# Revit family: Two Handle Lavatory Faucet_TOTO_TLG03201
name_source: partatom
category: 衛生器具
revit_build: Autodesk Revit 2018 (Build: 20181011_1500(x64)
units: mm (PartAtom-declared; Revit-internal decimal feet)

## family parameters
OmniClass タイトル = Sanitary, Laundry, and Cleaning Equipment
OmniClass 番号 = 23.45.00.00
パーツ タイプ = 標準
ロード時にボイドで切り取り = いいえ
丸型コネクタ寸法 = 直径を使用
作業面ベース = いいえ
共有 = いいえ
常に垂直 = はい
部屋計算ポイント = いいえ

## types (1)
- Two Handle Lavatory Faucet_TOTO_TLG03201
    Finish = faucet_material
    Height = 121.7
    Length = 179.4
    TOTO AsiaOceania = TLG03201B
    TOTO AsiaOceania URL = http://asia.toto.com
    TOTO China = TLG03201B
    TOTO China URL = http://www.toto.com.cn
    TOTO HongKong = TLG03201B
    TOTO HongKong URL = http://hk.toto.com
    TOTO India = TLG03201B
    TOTO India URL = https://in.toto.com
    TOTO Korea = TLG03201K
    TOTO Korea URL = https://kr.toto.com
    TOTO Taiwan = TLG03201B
    TOTO Taiwan URL = https://www.twtoto.com.tw
    TOTO Thailand = TLG03201T
    TOTO Thailand URL = https://th.toto.com
    TOTO USA = TLG03201U
    TOTO USA URL = https://www.totousa.com
    TOTO Vietnam = TLG03201B
    TOTO Vietnam URL = https://vn.toto.com
    Width = 341.1
    モデル = TLG03201
    製造元 = TOTO Ltd.
    説明 = Two Handle Lavatory Faucet/双柄双控洗面器水嘴

## geometry (parser evidence)
native form markers: Blend x2, Sweep x1
no freeform markers — native parametric forms only
